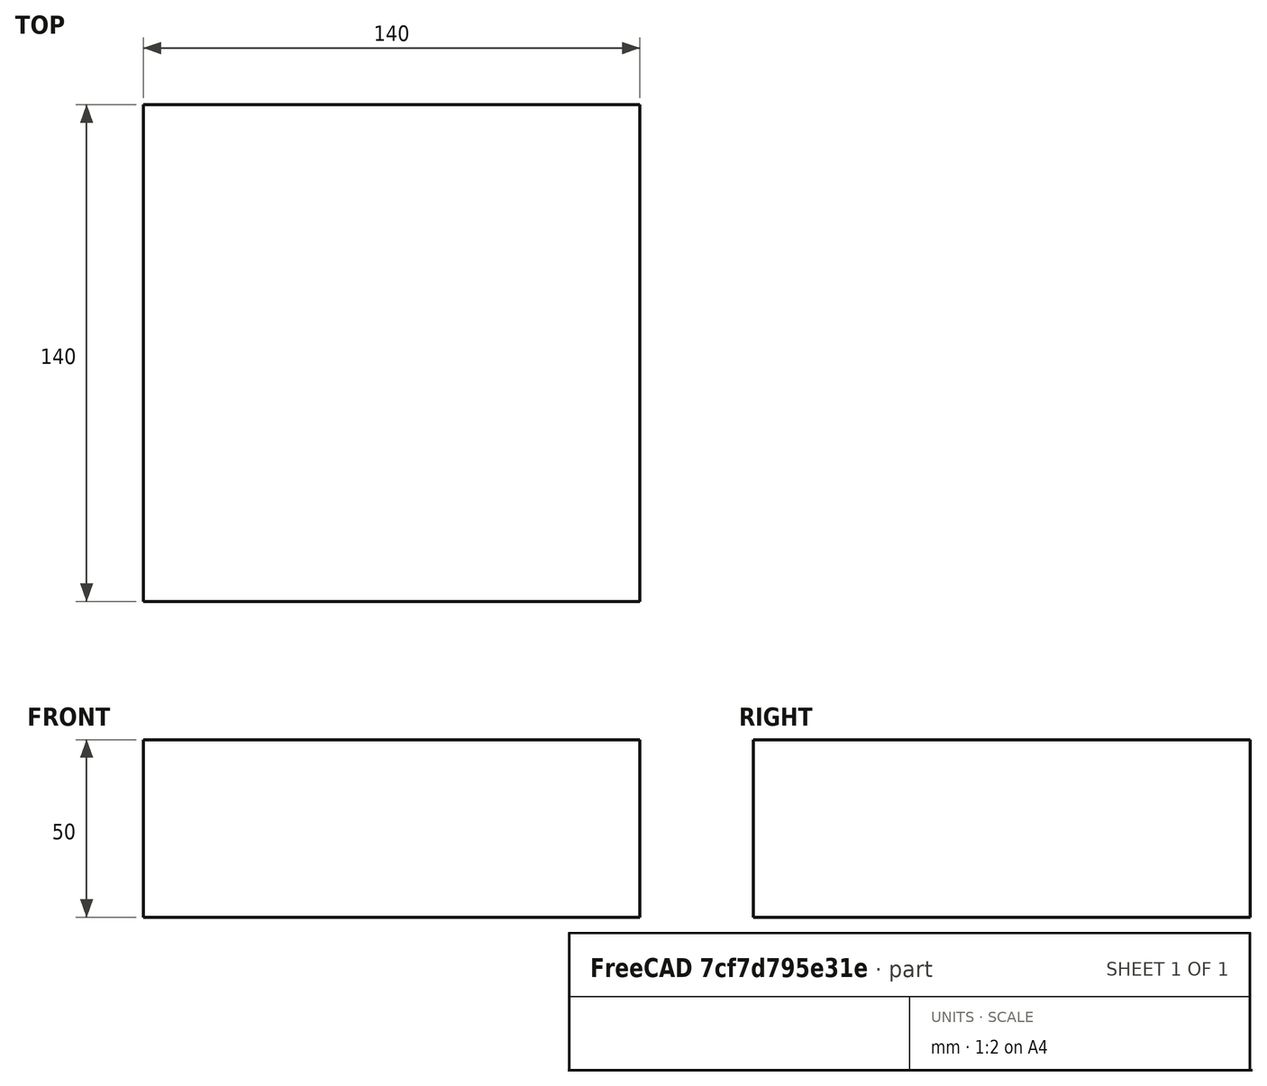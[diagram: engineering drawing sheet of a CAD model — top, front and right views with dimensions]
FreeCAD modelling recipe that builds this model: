
FCSTD DOCUMENT  (FreeCAD 0.15R4671 (Git))
Label: Square Bar 140 EN10059 S235JR
License: All rights reserved
LicenseURL: http://en.wikipedia.org/wiki/All_rights_reserved
objects: Sketcher::SketchObject×1, Part::Extrusion×1
note: 2 computed .brp shape members not serialized (recipe doc carries the construction recipe); baked Part::Feature solids carry a one-line shape summary decoded from their .brp

FEATURE [Sketcher::SketchObject] Sketch
  sketch-geometry (4):
    g0: LineSegment StartX=-70 StartY=-70 StartZ=0 EndX=70 EndY=-70 EndZ=0
    g1: LineSegment StartX=70 StartY=-70 StartZ=0 EndX=70 EndY=70 EndZ=0
    g2: LineSegment StartX=70 StartY=70 StartZ=0 EndX=-70 EndY=70 EndZ=0
    g3: LineSegment StartX=-70 StartY=70 StartZ=0 EndX=-70 EndY=-70 EndZ=0
  constraints (12):
    c: Coincident(g0,g1)
    c: Coincident(g1,g2)
    c: Coincident(g2,g3)
    c: Coincident(g3,g0)
    c: Horizontal(g0)
    c: Horizontal(g2)
    c: Vertical(g1)
    c: Vertical(g3)
    c: Symmetric(g1,g0,g-1)
    c: Symmetric(g2,g1,g-2)
    c: Equal(g1,g2)
    c: DistanceY(g1) = 140
FEATURE [Part::Extrusion] Extrude  label="Square Bar 140 EN10059 S235JR"
  Base = -> Sketch
  Dir = (0,0,50)
  Solid = true
